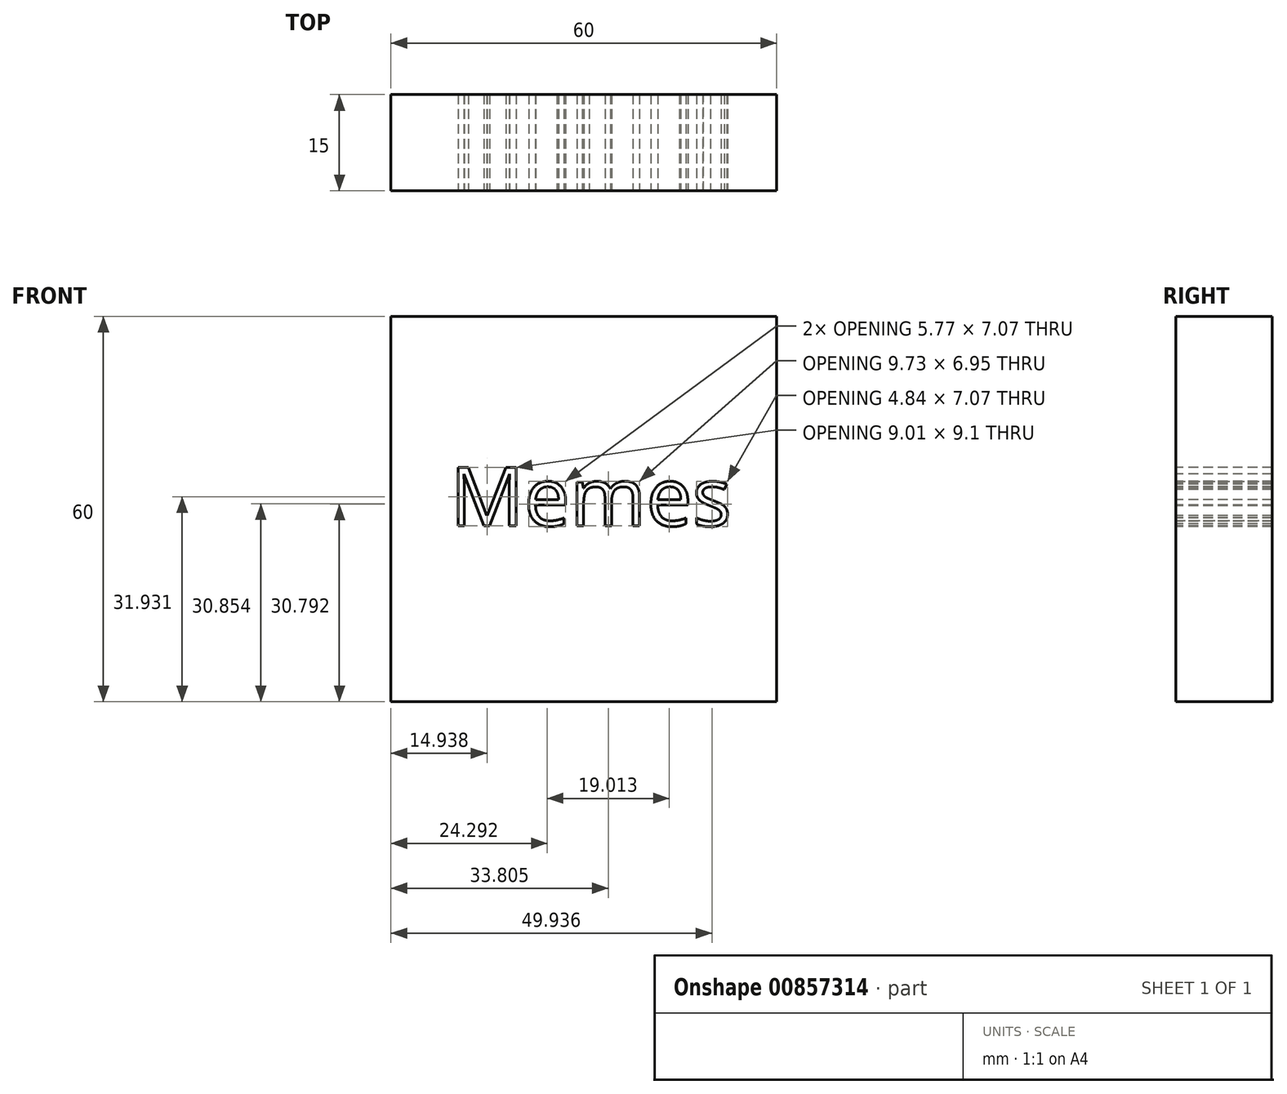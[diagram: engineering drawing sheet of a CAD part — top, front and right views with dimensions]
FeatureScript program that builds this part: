
annotation { "Feature Type Name" : "Feature", "Feature Type Description" : "" }
export const myFeature = defineFeature(function(context is Context, id is Id, definition is map)
    precondition{}
    {
        {
            var Q0;
            Q0=qCreatedBy(makeId("Front.planeOp"),FACE);
            var sketch = newSketch(context, id + "F0", { "sketchPlane" : qUnion([Q0])});
            skLineSegment(sketch, "E0", {"start": v(-37.75, 0) * mm, "end": v(-37.75, 60) * mm});
            skLineSegment(sketch, "E1", {"start": v(-37.75, 60) * mm, "end": v(22.25, 60) * mm});
            skLineSegment(sketch, "E2", {"start": v(22.25, 60) * mm, "end": v(22.25, 0) * mm});
            skLineSegment(sketch, "E3", {"start": v(22.25, 0) * mm, "end": v(-37.75, 0) * mm});
            skSolve(sketch);
        }
        {
            var Q0;
            Q0=makeQuery(id+"F0.imprint","IMPRINT",FACE,{"disambiguationData":[TD([[makeQuery(id+"F0.imprint","IMPRINT",EDGE,{"derivedFrom":sQuery(id+"F0.wireOp",EDGE,"E0")}),-1.0]])]});
            extrude(context, id + "F1", {"entities" : qUnion([Q0]), "depth" : 15 * mm, "offsetDistance" : 25 * mm});
        }
        {
            var Q0;
            Q0=makeQuery(id+"F1.opExtrude","CAP_FACE",FACE,{"disambiguationData":[OSD([sQuery(id+"F0.wireOp",EDGE,"E0"),sQuery(id+"F0.wireOp",EDGE,"E1"),sQuery(id+"F0.wireOp",EDGE,"E2"),sQuery(id+"F0.wireOp",EDGE,"E3")])],"isStart":false});
            var sketch = newSketch(context, id + "F2", { "sketchPlane" : qUnion([Q0])});
            skText(sketch, "E4", { "text": "Memes", "fontName": "OpenSans-Regular.ttf"});
            const initialGuessF2  = {"E4": [-0.02857, 0.02738, 1, 0, 0.00918]};
            skSetInitialGuess(sketch, initialGuessF2);
            skSolve(sketch);
        }
        {
            var Q0;
            Q0 = qSketchRegion(id + "F2", true);
            extrude(context, id + "F3", {"entities" : qUnion([Q0]), "operationType" : NewBodyOperationType.REMOVE, "oppositeDirection" : true, "depth" : 15 * mm, "offsetDistance" : 25 * mm});
        }
    });
